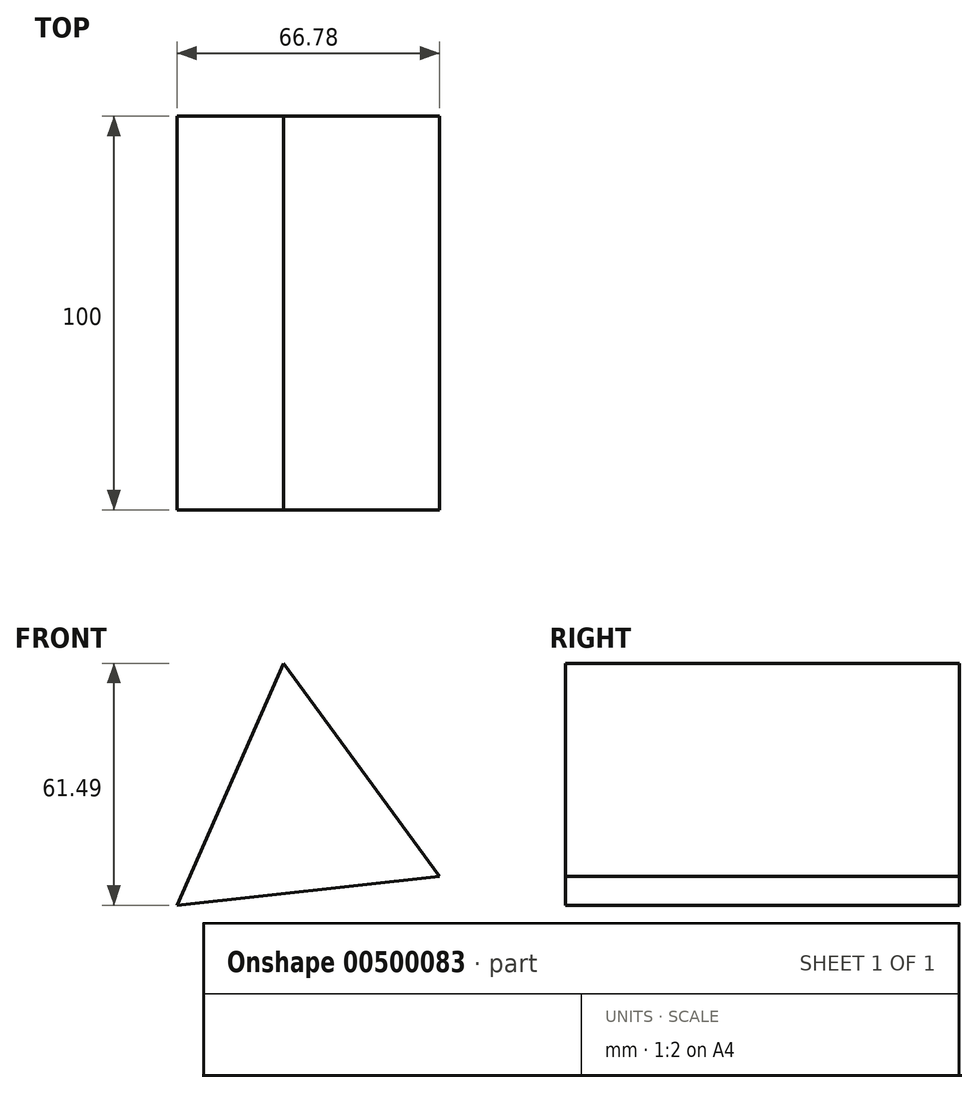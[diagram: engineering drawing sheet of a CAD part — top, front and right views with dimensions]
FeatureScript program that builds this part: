
annotation { "Feature Type Name" : "Feature", "Feature Type Description" : "" }
export const myFeature = defineFeature(function(context is Context, id is Id, definition is map)
    precondition{}
    {
        {
            var Q0;
            Q0=qCreatedBy(makeId("Front.planeOp"),FACE);
            var sketch = newSketch(context, id + "F0", { "sketchPlane" : qUnion([Q0])});
            skCircle(sketch, "E0.cCircle", {"center": v(0.58, 0) * mm, "radius": 38.79 * mm, "construction": true});
            skLineSegment(sketch, "E0.0", {"start": v(36.08, -15.63) * mm, "end": v(-30.7, -22.93) * mm});
            skLineSegment(sketch, "E0.1", {"start": v(-30.7, -22.93) * mm, "end": v(-3.63, 38.56) * mm});
            skLineSegment(sketch, "E0.2", {"start": v(-3.63, 38.56) * mm, "end": v(36.08, -15.63) * mm});
            skSolve(sketch);
        }
        {
            var Q0;
            Q0=makeQuery(id+"F0.imprint","IMPRINT",FACE,{"disambiguationData":[TD([[makeQuery(id+"F0.imprint","IMPRINT",EDGE,{"derivedFrom":sQuery(id+"F0.wireOp",EDGE,"E0.0")}),-1.0]])]});
            extrude(context, id + "F1", {"entities" : qUnion([Q0]), "endBound" : BoundingType.SYMMETRIC, "depth" : 100 * mm});
        }
    });
